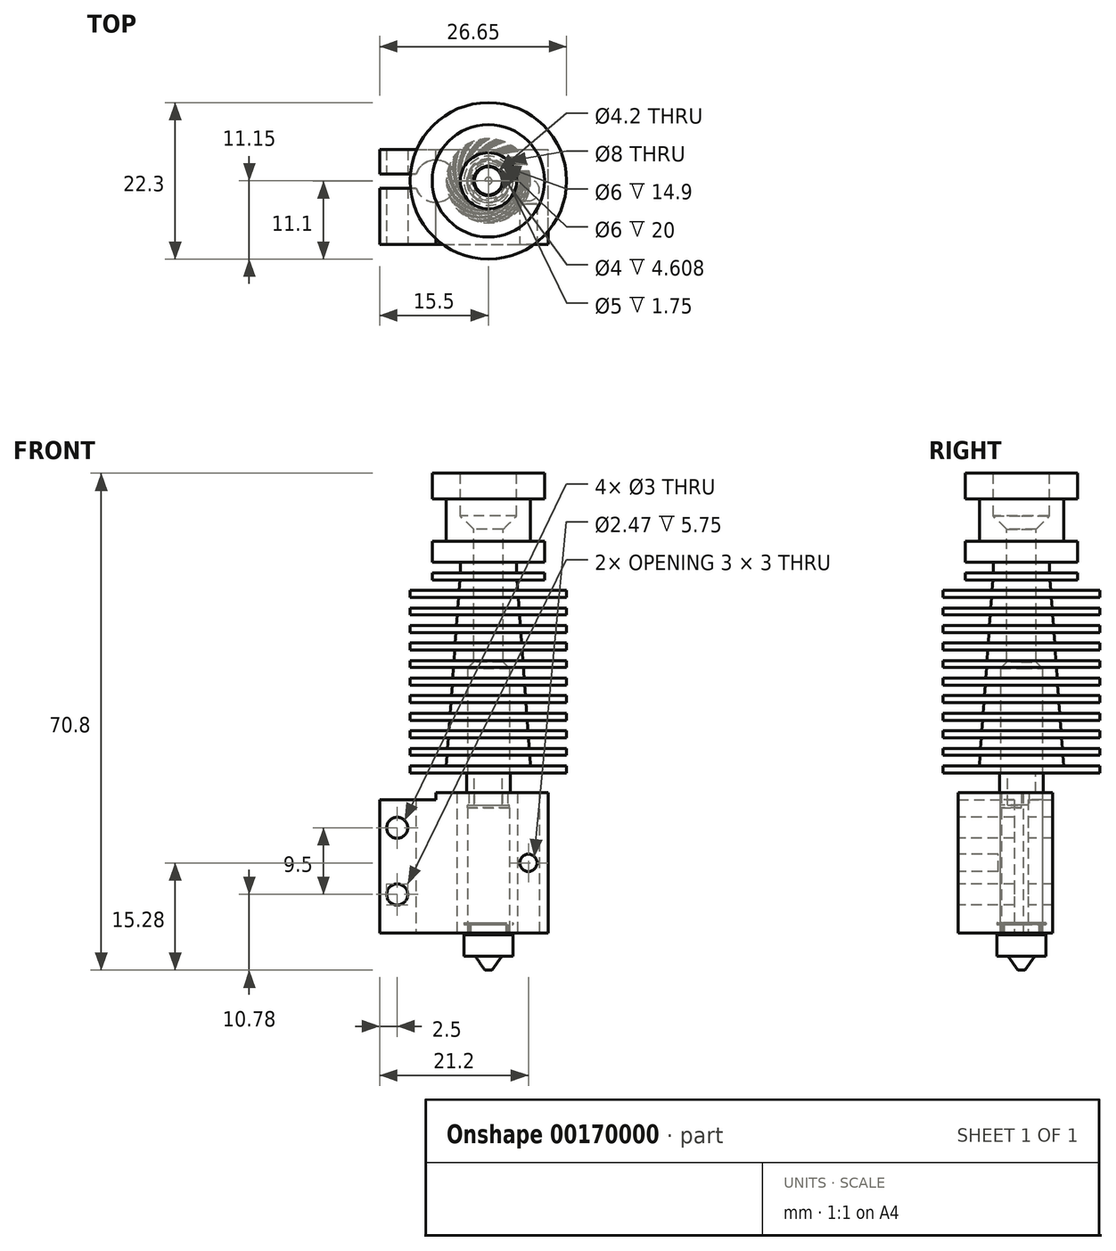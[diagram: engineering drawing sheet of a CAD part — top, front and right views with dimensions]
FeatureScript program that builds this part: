
annotation { "Feature Type Name" : "Feature", "Feature Type Description" : "" }
export const myFeature = defineFeature(function(context is Context, id is Id, definition is map)
    precondition{}
    {
        {
            var Q0;
            Q0=qCreatedBy(makeId("Top.planeOp"),FACE);
            var sketch = newSketch(context, id + "F0", { "sketchPlane" : qUnion([Q0])});
            skCircle(sketch, "E0", {"center": v(0, 0) * mm, "radius": 8 * mm});
            skSolve(sketch);
        }
        {
            var Q0;
            Q0=makeQuery(id+"F0.imprint","IMPRINT",FACE,{"disambiguationData":[TD([[makeQuery(id+"F0.imprint","IMPRINT",EDGE,{"derivedFrom":sQuery(id+"F0.wireOp",EDGE,"E0")}),1.0]])]});
            var Q1;
            Q1=sQuery(id+"F0.wireOp",EDGE,"E0");
            extrude(context, id + "F1", {"entities" : qUnion([Q0]), "surfaceEntities" : qUnion([Q1]), "oppositeDirection" : true, "depth" : 3.7 * mm});
        }
        {
            var Q0;
            Q0=makeQuery(id+"F1.opExtrude","CAP_FACE",FACE,{"disambiguationData":[OSD([sQuery(id+"F0.wireOp",EDGE,"E0")])],"isStart":false});
            var sketch = newSketch(context, id + "F2", { "sketchPlane" : qUnion([Q0])});
            skCircle(sketch, "E1", {"center": v(0, 0) * mm, "radius": 6 * mm});
            skSolve(sketch);
        }
        {
            var Q0;
            Q0=makeQuery(id+"F2.imprint","IMPRINT",FACE,{"disambiguationData":[TD([[makeQuery(id+"F2.imprint","IMPRINT",EDGE,{"derivedFrom":sQuery(id+"F2.wireOp",EDGE,"E1")}),1.0]])]});
            var Q1;
            Q1=sQuery(id+"F2.wireOp",EDGE,"E1");
            extrude(context, id + "F3", {"entities" : qUnion([Q0]), "operationType" : NewBodyOperationType.ADD, "surfaceEntities" : qUnion([Q1]), "depth" : 6 * mm});
        }
        {
            var Q0;
            Q0=makeQuery(id+"F3.opExtrude","CAP_FACE",FACE,{"disambiguationData":[OSD([sQuery(id+"F2.wireOp",EDGE,"E1")])],"isStart":false});
            var sketch = newSketch(context, id + "F4", { "sketchPlane" : qUnion([Q0])});
            skCircle(sketch, "E2", {"center": v(0, 0) * mm, "radius": 8 * mm});
            skSolve(sketch);
        }
        {
            var Q0;
            Q0=qSketchRegion(id+"F4",true);
            extrude(context, id + "F5", {"entities" : qUnion([Q0]), "operationType" : NewBodyOperationType.ADD, "depth" : 3 * mm});
        }
        {
            var Q0;
            Q0=qCreatedBy(makeId("Front.planeOp"),FACE);
            var sketch = newSketch(context, id + "F6", { "sketchPlane" : qUnion([Q0])});
            skLineSegment(sketch, "E3", {"start": v(0, 0) * mm, "end": v(0, -12.7) * mm});
            skLineSegment(sketch, "E4.bottom", {"start": v(0, -12.7) * mm, "end": v(4, -12.7) * mm});
            skLineSegment(sketch, "E4.top", {"start": v(0, -14.2) * mm, "end": v(4, -14.2) * mm});
            skLineSegment(sketch, "E4.left", {"start": v(0, -12.7) * mm, "end": v(0, -14.2) * mm});
            skLineSegment(sketch, "E4.right", {"start": v(4, -12.7) * mm, "end": v(4, -14.2) * mm});
            skLineSegment(sketch, "E5.bottom", {"start": v(0, -14.2) * mm, "end": v(8, -14.2) * mm});
            skLineSegment(sketch, "E5.top", {"start": v(0, -15.2) * mm, "end": v(8, -15.2) * mm});
            skLineSegment(sketch, "E5.left", {"start": v(0, -14.2) * mm, "end": v(0, -15.2) * mm});
            skLineSegment(sketch, "E5.right", {"start": v(8, -14.2) * mm, "end": v(8, -15.2) * mm});
            skLineSegment(sketch, "E6", {"start": v(0, -15.2) * mm, "end": v(0, -16.7) * mm});
            skLineSegment(sketch, "E7.bottom", {"start": v(0, -16.7) * mm, "end": v(11.15, -16.7) * mm});
            skLineSegment(sketch, "E7.top", {"start": v(0, -17.7) * mm, "end": v(11.15, -17.7) * mm});
            skLineSegment(sketch, "E7.left", {"start": v(0, -16.7) * mm, "end": v(0, -17.7) * mm});
            skLineSegment(sketch, "E7.right", {"start": v(11.15, -16.7) * mm, "end": v(11.15, -17.7) * mm});
            skLineSegment(sketch, "E8.1.0.0", {"start": v(0, -20.2) * mm, "end": v(11.15, -20.2) * mm});
            skLineSegment(sketch, "E8.1.0.1", {"start": v(0, -19.2) * mm, "end": v(11.15, -19.2) * mm});
            skLineSegment(sketch, "E8.1.0.2", {"start": v(0, -19.2) * mm, "end": v(0, -20.2) * mm});
            skLineSegment(sketch, "E8.1.0.3", {"start": v(11.15, -19.2) * mm, "end": v(11.15, -20.2) * mm});
            skLineSegment(sketch, "E8.2.0.0", {"start": v(0, -22.7) * mm, "end": v(11.15, -22.7) * mm});
            skLineSegment(sketch, "E8.2.0.1", {"start": v(0, -21.7) * mm, "end": v(11.15, -21.7) * mm});
            skLineSegment(sketch, "E8.2.0.2", {"start": v(0, -21.7) * mm, "end": v(0, -22.7) * mm});
            skLineSegment(sketch, "E8.2.0.3", {"start": v(11.15, -21.7) * mm, "end": v(11.15, -22.7) * mm});
            skLineSegment(sketch, "E8.3.0.0", {"start": v(0, -25.2) * mm, "end": v(11.15, -25.2) * mm});
            skLineSegment(sketch, "E8.3.0.1", {"start": v(0, -24.2) * mm, "end": v(11.15, -24.2) * mm});
            skLineSegment(sketch, "E8.3.0.2", {"start": v(0, -24.2) * mm, "end": v(0, -25.2) * mm});
            skLineSegment(sketch, "E8.3.0.3", {"start": v(11.15, -24.2) * mm, "end": v(11.15, -25.2) * mm});
            skLineSegment(sketch, "E8.4.0.0", {"start": v(0, -27.7) * mm, "end": v(11.15, -27.7) * mm});
            skLineSegment(sketch, "E8.4.0.1", {"start": v(0, -26.7) * mm, "end": v(11.15, -26.7) * mm});
            skLineSegment(sketch, "E8.4.0.2", {"start": v(0, -26.7) * mm, "end": v(0, -27.7) * mm});
            skLineSegment(sketch, "E8.4.0.3", {"start": v(11.15, -26.7) * mm, "end": v(11.15, -27.7) * mm});
            skLineSegment(sketch, "E8.5.0.0", {"start": v(0, -30.2) * mm, "end": v(11.15, -30.2) * mm});
            skLineSegment(sketch, "E8.5.0.1", {"start": v(0, -29.2) * mm, "end": v(11.15, -29.2) * mm});
            skLineSegment(sketch, "E8.5.0.2", {"start": v(0, -29.2) * mm, "end": v(0, -30.2) * mm});
            skLineSegment(sketch, "E8.5.0.3", {"start": v(11.15, -29.2) * mm, "end": v(11.15, -30.2) * mm});
            skLineSegment(sketch, "E8.6.0.0", {"start": v(0, -32.7) * mm, "end": v(11.15, -32.7) * mm});
            skLineSegment(sketch, "E8.6.0.1", {"start": v(0, -31.7) * mm, "end": v(11.15, -31.7) * mm});
            skLineSegment(sketch, "E8.6.0.2", {"start": v(0, -31.7) * mm, "end": v(0, -32.7) * mm});
            skLineSegment(sketch, "E8.6.0.3", {"start": v(11.15, -31.7) * mm, "end": v(11.15, -32.7) * mm});
            skLineSegment(sketch, "E8.7.0.0", {"start": v(0, -35.2) * mm, "end": v(11.15, -35.2) * mm});
            skLineSegment(sketch, "E8.7.0.1", {"start": v(0, -34.2) * mm, "end": v(11.15, -34.2) * mm});
            skLineSegment(sketch, "E8.7.0.2", {"start": v(0, -34.2) * mm, "end": v(0, -35.2) * mm});
            skLineSegment(sketch, "E8.7.0.3", {"start": v(11.15, -34.2) * mm, "end": v(11.15, -35.2) * mm});
            skLineSegment(sketch, "E8.8.0.0", {"start": v(0, -37.7) * mm, "end": v(11.15, -37.7) * mm});
            skLineSegment(sketch, "E8.8.0.1", {"start": v(0, -36.7) * mm, "end": v(11.15, -36.7) * mm});
            skLineSegment(sketch, "E8.8.0.2", {"start": v(0, -36.7) * mm, "end": v(0, -37.7) * mm});
            skLineSegment(sketch, "E8.8.0.3", {"start": v(11.15, -36.7) * mm, "end": v(11.15, -37.7) * mm});
            skLineSegment(sketch, "E8.9.0.0", {"start": v(0, -40.2) * mm, "end": v(11.15, -40.2) * mm});
            skLineSegment(sketch, "E8.9.0.1", {"start": v(0, -39.2) * mm, "end": v(11.15, -39.2) * mm});
            skLineSegment(sketch, "E8.9.0.2", {"start": v(0, -39.2) * mm, "end": v(0, -40.2) * mm});
            skLineSegment(sketch, "E8.9.0.3", {"start": v(11.15, -39.2) * mm, "end": v(11.15, -40.2) * mm});
            skLineSegment(sketch, "E8.10.0.0", {"start": v(0, -42.7) * mm, "end": v(11.15, -42.7) * mm});
            skLineSegment(sketch, "E8.10.0.1", {"start": v(0, -41.7) * mm, "end": v(11.15, -41.7) * mm});
            skLineSegment(sketch, "E8.10.0.2", {"start": v(0, -41.7) * mm, "end": v(0, -42.7) * mm});
            skLineSegment(sketch, "E8.10.0.3", {"start": v(11.15, -41.7) * mm, "end": v(11.15, -42.7) * mm});
            skLineSegment(sketch, "E8.direction1", {"start": v(0, -17.7) * mm, "end": v(0, -20.2) * mm, "construction": true});
            skLineSegment(sketch, "E9", {"start": v(0, -41.7) * mm, "end": v(6, -41.7) * mm});
            skLineSegment(sketch, "E10", {"start": v(4.07, -15.2) * mm, "end": v(4.18, -16.7) * mm});
            skLineSegment(sketch, "E11.trimOffspring", {"start": v(4.25, -17.7) * mm, "end": v(4.36, -19.2) * mm});
            skLineSegment(sketch, "E12.trimOffspring", {"start": v(4.44, -20.2) * mm, "end": v(4.55, -21.7) * mm});
            skLineSegment(sketch, "E13.trimOffspring", {"start": v(4.62, -22.7) * mm, "end": v(4.73, -24.2) * mm});
            skLineSegment(sketch, "E14.trimOffspring", {"start": v(4.8, -25.2) * mm, "end": v(4.9, -26.7) * mm});
            skLineSegment(sketch, "E15.trimOffspring", {"start": v(4.98, -27.7) * mm, "end": v(5.1, -29.2) * mm});
            skLineSegment(sketch, "E16.trimOffspring", {"start": v(5.16, -30.2) * mm, "end": v(5.27, -31.7) * mm});
            skLineSegment(sketch, "E17.trimOffspring", {"start": v(5.35, -32.7) * mm, "end": v(5.45, -34.2) * mm});
            skLineSegment(sketch, "E18.trimOffspring", {"start": v(5.53, -35.2) * mm, "end": v(5.64, -36.7) * mm});
            skLineSegment(sketch, "E19.trimOffspring", {"start": v(5.7, -37.7) * mm, "end": v(5.82, -39.2) * mm});
            skLineSegment(sketch, "E20.trimOffspring", {"start": v(5.9, -40.2) * mm, "end": v(6, -41.7) * mm});
            skLineSegment(sketch, "E21", {"start": v(0, -17.7) * mm, "end": v(0, -19.2) * mm});
            skLineSegment(sketch, "E22", {"start": v(0, -20.2) * mm, "end": v(0, -21.7) * mm});
            skLineSegment(sketch, "E23", {"start": v(0, -22.7) * mm, "end": v(0, -24.2) * mm});
            skLineSegment(sketch, "E24", {"start": v(0, -25.2) * mm, "end": v(0, -26.7) * mm});
            skLineSegment(sketch, "E25", {"start": v(0, -27.7) * mm, "end": v(0, -29.2) * mm});
            skLineSegment(sketch, "E26", {"start": v(0, -30.2) * mm, "end": v(0, -31.7) * mm});
            skLineSegment(sketch, "E27", {"start": v(0, -32.7) * mm, "end": v(0, -34.2) * mm});
            skLineSegment(sketch, "E28", {"start": v(0, -35.2) * mm, "end": v(0, -36.7) * mm});
            skLineSegment(sketch, "E29", {"start": v(0, -37.7) * mm, "end": v(0, -39.2) * mm});
            skLineSegment(sketch, "E30", {"start": v(0, -40.2) * mm, "end": v(0, -41.7) * mm});
            skLineSegment(sketch, "E31.right", {"start": v(3, -42.7) * mm, "end": v(3, -45.2) * mm});
            skLineSegment(sketch, "E32", {"start": v(3, -45.2) * mm, "end": v(2, -45.2) * mm});
            skLineSegment(sketch, "E33", {"start": v(2, -45.2) * mm, "end": v(2, -42.7) * mm});
            skLineSegment(sketch, "E34.bottom", {"start": v(2, -45.2) * mm, "end": v(3, -45.2) * mm});
            skLineSegment(sketch, "E34.top", {"start": v(2, -47.3) * mm, "end": v(3, -47.3) * mm});
            skLineSegment(sketch, "E34.left", {"start": v(2, -45.2) * mm, "end": v(2, -47.3) * mm});
            skLineSegment(sketch, "E34.right", {"start": v(3, -45.2) * mm, "end": v(3, -47.3) * mm});
            skLineSegment(sketch, "E35.bottom", {"start": v(3, -47.3) * mm, "end": v(3.75, -47.3) * mm});
            skLineSegment(sketch, "E35.top", {"start": v(3, -46.56) * mm, "end": v(3.75, -46.56) * mm});
            skLineSegment(sketch, "E35.left", {"start": v(3, -47.3) * mm, "end": v(3, -46.56) * mm});
            skLineSegment(sketch, "E35.right", {"start": v(3.75, -47.3) * mm, "end": v(3.75, -46.56) * mm});
            skLineSegment(sketch, "E36.bottom", {"start": v(2, -42.7) * mm, "end": v(3, -42.7) * mm});
            skLineSegment(sketch, "E36.top", {"start": v(2, -41.7) * mm, "end": v(3, -41.7) * mm});
            skLineSegment(sketch, "E36.left", {"start": v(2, -42.7) * mm, "end": v(2, -41.7) * mm});
            skLineSegment(sketch, "E36.right", {"start": v(3, -42.7) * mm, "end": v(3, -41.7) * mm});
            skSolve(sketch);
        }
        {
            var Q0;
            Q0=qSketchRegion(id+"F6",true);
            var Q1;
            {var subQ0=sQuery(id+"F6.wireOp",EDGE,"E31.right");Q1=makeQuery(id+"F6.imprint","IMPRINT",FACE,{"disambiguationData":[TD([[makeQuery(id+"F6.imprint","IMPRINT",EDGE,{"derivedFrom":subQ0}),-1.0]])]});}
            var Q2;
            Q2=makeQuery(id+"F6.imprint","IMPRINT",FACE,{"disambiguationData":[TD([[makeQuery(id+"F6.imprint","IMPRINT",EDGE,{"derivedFrom":sQuery(id+"F6.wireOp",EDGE,"E34.bottom")}),-1.0]])]});
            var Q3;
            Q3=makeQuery(id+"F6.imprint","IMPRINT",FACE,{"disambiguationData":[TD([[makeQuery(id+"F6.imprint","IMPRINT",EDGE,{"derivedFrom":sQuery(id+"F6.wireOp",EDGE,"E36.bottom")}),1.0]])]});
            var Q4;
            Q4=makeQuery(id+"F6.imprint","IMPRINT",FACE,{"disambiguationData":[TD([[makeQuery(id+"F6.imprint","IMPRINT",EDGE,{"derivedFrom":sQuery(id+"F6.wireOp",EDGE,"E31.right")}),-1.0]])]});
            var Q5;
            Q5=makeQuery(id+"F6.imprint","IMPRINT",FACE,{"disambiguationData":[TD([[makeQuery(id+"F6.imprint","IMPRINT",EDGE,{"derivedFrom":sQuery(id+"F6.wireOp",EDGE,"E34.bottom")}),-1.0]])]});
            var Q6;
            Q6=sQuery(id+"F6.wireOp",EDGE,"E3");
            revolve(context, id + "F7", {"operationType" : NewBodyOperationType.ADD, "entities" : qUnion([Q0, Q1, Q2, Q3, Q4, Q5]), "axis" : qUnion([Q6]), "revolveType" : RevolveType.FULL});
        }
        {
            var Q0;
            Q0=makeQuery(id+"F1.opExtrude","CAP_FACE",FACE,{"disambiguationData":[OSD([sQuery(id+"F0.wireOp",EDGE,"E0")])],"isStart":true});
            var sketch = newSketch(context, id + "F8", { "sketchPlane" : qUnion([Q0])});
            skCircle(sketch, "E37", {"center": v(0, 0) * mm, "radius": 2.1 * mm});
            skSolve(sketch);
        }
        {
            var Q0;
            Q0=qSketchRegion(id+"F8",true);
            extrude(context, id + "F9", {"entities" : qUnion([Q0]), "operationType" : NewBodyOperationType.REMOVE, "oppositeDirection" : true, "depth" : 42.7 * mm});
        }
        {
            var Q0;
            Q0=makeQuery(id+"F1.opExtrude","CAP_FACE",FACE,{"disambiguationData":[OSD([sQuery(id+"F0.wireOp",EDGE,"E0")])],"isStart":true});
            var sketch = newSketch(context, id + "F10", { "sketchPlane" : qUnion([Q0])});
            skCircle(sketch, "E38", {"center": v(0, 0) * mm, "radius": 4 * mm});
            skSolve(sketch);
        }
        {
            var Q0;
            Q0=qSketchRegion(id+"F10",true);
            extrude(context, id + "F11", {"entities" : qUnion([Q0]), "operationType" : NewBodyOperationType.REMOVE, "oppositeDirection" : true, "depth" : 6 * mm});
        }
        {
            var Q0;
            Q0=makeQuery(id+"F11.boolean.opBoolean","INTERSECT",EDGE,{"derivedFrom":[makeQuery(id+"F9.boolean.opBoolean","COPY",FACE,{"derivedFrom":makeQuery(id+"F9.opExtrude","SWEPT_FACE",FACE,{"disambiguationData":[OSD([sQuery(id+"F8.wireOp",EDGE,"E37")])]})}),makeQuery(id+"F11.opExtrude","CAP_FACE",FACE,{"disambiguationData":[OSD([sQuery(id+"F10.wireOp",EDGE,"E38")])],"isStart":false})]});
            chamfer(context, id + "F12", {"entities" : qUnion([Q0]), "width" : 2 * mm, "tangentPropagation" : true});
        }
        {
            var Q0;
            Q0=makeQuery(id+"F7.opRevolve","SWEPT_FACE",FACE,{"disambiguationData":[OSD([sQuery(id+"F6.wireOp",EDGE,"E8.10.0.0")])]});
            var sketch = newSketch(context, id + "F13", { "sketchPlane" : qUnion([Q0])});
            skCircle(sketch, "E39", {"center": v(0, 0) * mm, "radius": 3 * mm});
            skSolve(sketch);
        }
        {
            var Q0;
            Q0=qSketchRegion(id+"F13",true);
            extrude(context, id + "F14", {"entities" : qUnion([Q0]), "operationType" : NewBodyOperationType.REMOVE, "oppositeDirection" : true, "depth" : 14.8 * mm});
        }
        {
            var Q0;
            Q0=makeQuery(id+"F14.boolean.opBoolean","INTERSECT",EDGE,{"derivedFrom":[makeQuery(id+"F9.boolean.opBoolean","COPY",FACE,{"derivedFrom":makeQuery(id+"F9.opExtrude","SWEPT_FACE",FACE,{"disambiguationData":[OSD([sQuery(id+"F8.wireOp",EDGE,"E37")])]})}),makeQuery(id+"F14.opExtrude","CAP_FACE",FACE,{"disambiguationData":[OSD([sQuery(id+"F13.wireOp",EDGE,"E39")])],"isStart":false})]});
            chamfer(context, id + "F15", {"entities" : qUnion([Q0]), "width" : 1 * mm, "tangentPropagation" : true});
        }
        {
            var Q0;
            Q0=qCreatedBy(makeId("Front.planeOp"),FACE);
            var sketch = newSketch(context, id + "F16", { "sketchPlane" : qUnion([Q0])});
            skLineSegment(sketch, "E40.bottom", {"start": v(-7.5, -45.52) * mm, "end": v(8.5, -45.52) * mm});
            skLineSegment(sketch, "E40.top", {"start": v(-15.5, -65.52) * mm, "end": v(8.5, -65.52) * mm});
            skLineSegment(sketch, "E40.right", {"start": v(8.5, -45.52) * mm, "end": v(8.5, -65.52) * mm});
            skLineSegment(sketch, "E41", {"start": v(-15.5, -46.52) * mm, "end": v(-15.5, -65.52) * mm});
            skLineSegment(sketch, "E42", {"start": v(-7.5, -45.52) * mm, "end": v(-7.5, -46.52) * mm});
            skLineSegment(sketch, "E43", {"start": v(-15.5, -46.52) * mm, "end": v(-7.5, -46.52) * mm});
            skSolve(sketch);
        }
        {
            var Q0;
            Q0=makeQuery(id+"F16.imprint","IMPRINT",FACE,{"disambiguationData":[TD([[makeQuery(id+"F16.imprint","IMPRINT",EDGE,{"derivedFrom":sQuery(id+"F16.wireOp",EDGE,"E40.bottom")}),-1.0]])]});
            var Q1;
            Q1=makeQuery(id+"F16.imprint","IMPRINT",FACE,{"disambiguationData":[TD([[makeQuery(id+"F16.imprint","IMPRINT",EDGE,{"derivedFrom":sQuery(id+"F16.wireOp",EDGE,"hSTLO5rz-Z077-ZaO5-nEVS-phWlFBx8dYmu")}),1.0]])]});
            var Q2;
            Q2=makeQuery(id+"F16.imprint","IMPRINT",FACE,{"disambiguationData":[TD([[makeQuery(id+"F16.imprint","IMPRINT",EDGE,{"derivedFrom":sQuery(id+"F16.wireOp",EDGE,"1ucrc5hz-Jwvr-DOmE-K7qY-mdj6J8iSEPF0")}),1.0]])]});
            extrude(context, id + "F17", {"entities" : qUnion([Q0, Q1, Q2]), "depth" : 13.5 * mm, "symmetric" : true});
        }
        {
            var Q0;
            Q0=makeQuery(id+"F17.opExtrude","SWEPT_FACE",FACE,{"disambiguationData":[OSD([sQuery(id+"F16.wireOp",EDGE,"E40.top")])]});
            var sketch = newSketch(context, id + "F18", { "sketchPlane" : qUnion([Q0])});
            skCircle(sketch, "E44", {"center": v(0, -2.25) * mm, "radius": 3 * mm});
            skCircle(sketch, "E45", {"center": v(5.7, -1) * mm, "radius": 1.55 * mm});
            skArc(sketch, "E46", {"start": v(-10.33, -3.25) * mm, "mid": v(-4.5, -2.25) * mm, "end": v(-10.33, -1.25) * mm});
            skLineSegment(sketch, "E47.bottom", {"start": v(-15.5, -1.25) * mm, "end": v(-10.33, -1.25) * mm});
            skLineSegment(sketch, "E47.top", {"start": v(-15.5, -3.25) * mm, "end": v(-10.33, -3.25) * mm});
            skLineSegment(sketch, "E47.left", {"start": v(-15.5, -1.25) * mm, "end": v(-15.5, -3.25) * mm});
            skSolve(sketch);
        }
        {
            var Q0;
            Q0 = qSketchRegion(id + "F18", true);
            extrude(context, id + "F19", {"entities" : qUnion([Q0]), "operationType" : NewBodyOperationType.REMOVE, "oppositeDirection" : true, "depth" : 20 * mm});
        }
        {
            var Q0;
            Q0=makeQuery(id+"F17.opExtrude","SWEPT_BODY",BODY,{"disambiguationData":[OSD([sQuery(id+"F16.wireOp",EDGE,"E40.bottom"),sQuery(id+"F16.wireOp",EDGE,"E40.top"),sQuery(id+"F16.wireOp",EDGE,"E40.right"),sQuery(id+"F16.wireOp",EDGE,"E41"),sQuery(id+"F16.wireOp",EDGE,"E42"),sQuery(id+"F16.wireOp",EDGE,"E43")])]});
            var Q1;
            Q1=qCreatedBy(makeId("Origin.pointOp"),VERTEX);
            var Q2;
            Q2=makeQuery(id+"F19.boolean.opBoolean","COPY",EDGE,{"derivedFrom":makeQuery(id+"F19.opExtrude","CAP_EDGE",EDGE,{"disambiguationData":[OSD([sQuery(id+"F18.wireOp",EDGE,"E44")])],"isStart":true})});
            var Q3;
            Q3=qCreatedBy(makeId("Front.planeOp"),FACE);
            transform(context, id + "F20", {"entities" : qUnion([Q0]), "transformType" : TransformType.TRANSLATION_DISTANCE, "transformDirection" : qUnion([Q3]), "distance" : 2.3 * mm, "makeCopy" : false});
        }
        {
            var Q0;
            Q0=qCreatedBy(makeId("Front.planeOp"),FACE);
            var sketch = newSketch(context, id + "F21", { "sketchPlane" : qUnion([Q0])});
            skLineSegment(sketch, "E48.bottom", {"start": v(0, -65.8) * mm, "end": v(3.5, -65.8) * mm});
            skLineSegment(sketch, "E48.right", {"start": v(3.5, -65.8) * mm, "end": v(3.5, -68.8) * mm});
            skLineSegment(sketch, "E49.top", {"start": v(0, -70.8) * mm, "end": v(0.5, -70.8) * mm});
            skLineSegment(sketch, "E50", {"start": v(0.5, -70.8) * mm, "end": v(1.9, -68.8) * mm});
            skLineSegment(sketch, "E51.trimOffspring", {"start": v(1.9, -68.8) * mm, "end": v(3.5, -68.8) * mm});
            skLineSegment(sketch, "E52", {"start": v(0, -70.8) * mm, "end": v(0, -65.8) * mm});
            skLineSegment(sketch, "E53", {"start": v(0, -65.8) * mm, "end": v(2.5, -65.8) * mm});
            skLineSegment(sketch, "E54", {"start": v(2.5, -65.8) * mm, "end": v(2.5, -64.3) * mm});
            skLineSegment(sketch, "E55", {"start": v(2.5, -64.3) * mm, "end": v(2.75, -64.3) * mm});
            skLineSegment(sketch, "E56", {"start": v(2.75, -64.3) * mm, "end": v(2.75, -65.8) * mm});
            skLineSegment(sketch, "E57.bottom", {"start": v(2.5, -64.3) * mm, "end": v(3.5, -64.3) * mm});
            skLineSegment(sketch, "E57.top", {"start": v(2.5, -64.05) * mm, "end": v(3.5, -64.05) * mm});
            skLineSegment(sketch, "E57.left", {"start": v(2.5, -64.3) * mm, "end": v(2.5, -64.05) * mm});
            skLineSegment(sketch, "E57.right", {"start": v(3.5, -64.3) * mm, "end": v(3.5, -64.05) * mm});
            skSolve(sketch);
        }
        {
            var Q0;
            Q0 = qSketchRegion(id + "F21", true);
            var Q1;
            Q1=sQuery(id+"F21.wireOp",EDGE,"E52");
            revolve(context, id + "F22", {"entities" : qUnion([Q0]), "axis" : qUnion([Q1]), "revolveType" : RevolveType.FULL});
        }
        {
            var Q0;
            Q0=makeQuery(id+"F17.opExtrude","CAP_FACE",FACE,{"disambiguationData":[OSD([sQuery(id+"F16.wireOp",EDGE,"E40.bottom"),sQuery(id+"F16.wireOp",EDGE,"E40.top"),sQuery(id+"F16.wireOp",EDGE,"E40.left"),sQuery(id+"F16.wireOp",EDGE,"E40.right"),sQuery(id+"F16.wireOp",EDGE,"UV7SLQof-a04S-M22U-fSmA-h1v0EtluGPG8"),sQuery(id+"F16.wireOp",EDGE,"g7xF2yxM-ANDZ-qpWR-qvBO-6FQJMMhnbeDq.top"),sQuery(id+"F16.wireOp",EDGE,"L5R9zHDy-imt3-tSqA-0CQm-Dj3PFv1zczeX.top"),sQuery(id+"F16.wireOp",EDGE,"56c6f5e6-72b2-44f0-a3dc-ebd65ac1d403.trimOffspring")])],"isStart":false});
            var sketch = newSketch(context, id + "F23", { "sketchPlane" : qUnion([Q0])});
            skCircle(sketch, "E58", {"center": v(-13, -60.02) * mm, "radius": 1.5 * mm});
            skCircle(sketch, "E59", {"center": v(-13, -50.52) * mm, "radius": 1.5 * mm});
            skCircle(sketch, "E60", {"center": v(5.7, -55.52) * mm, "radius": 1.23 * mm});
            skSolve(sketch);
        }
        {
            var Q0;
            Q0=makeQuery(id+"F23.imprint","IMPRINT",FACE,{"disambiguationData":[TD([[makeQuery(id+"F23.imprint","IMPRINT",EDGE,{"derivedFrom":sQuery(id+"F23.wireOp",EDGE,"E60")}),1.0]])]});
            extrude(context, id + "F24", {"entities" : qUnion([Q0]), "operationType" : NewBodyOperationType.REMOVE, "oppositeDirection" : true, "depth" : 5.75 * mm});
        }
        {
            var Q0;
            Q0=makeQuery(id+"F23.imprint","IMPRINT",FACE,{"disambiguationData":[TD([[makeQuery(id+"F23.imprint","IMPRINT",EDGE,{"derivedFrom":sQuery(id+"F23.wireOp",EDGE,"E59")}),1.0]])]});
            var Q1;
            Q1=makeQuery(id+"F23.imprint","IMPRINT",FACE,{"disambiguationData":[TD([[makeQuery(id+"F23.imprint","IMPRINT",EDGE,{"derivedFrom":sQuery(id+"F23.wireOp",EDGE,"E58")}),1.0]])]});
            var Q2;
            Q2=makeQuery(id+"F17.opExtrude","CAP_FACE",FACE,{"disambiguationData":[OSD([sQuery(id+"F16.wireOp",EDGE,"E40.bottom"),sQuery(id+"F16.wireOp",EDGE,"E40.top"),sQuery(id+"F16.wireOp",EDGE,"E40.right"),sQuery(id+"F16.wireOp",EDGE,"E41"),sQuery(id+"F16.wireOp",EDGE,"E42"),sQuery(id+"F16.wireOp",EDGE,"E43")])],"isStart":true});
            extrude(context, id + "F25", {"entities" : qUnion([Q0, Q1]), "operationType" : NewBodyOperationType.REMOVE, "endBound" : BoundingType.UP_TO_SURFACE, "oppositeDirection" : true, "endBoundEntityFace" : qUnion([Q2]), "depth" : 4.5 * mm});
        }
        {
            var Q0;
            {var subQ0=sQuery(id+"F6.wireOp",EDGE,"E8.10.0.0");Q0=makeQuery(id+"F7.opRevolve","SWEPT_FACE",FACE,{"disambiguationData":[OSD([subQ0]),TDD([makeQuery(id+"F6.imprint","IMPRINT",EDGE,{"disambiguationData":[TD([[makeQuery(id+"F6.imprint","INTERSECT",VERTEX,{"derivedFrom":[subQ0,sQuery(id+"F6.wireOp",EDGE,"E8.10.0.3")]}),1.0]])],"derivedFrom":subQ0})])]});}
            var sketch = newSketch(context, id + "F26", { "sketchPlane" : qUnion([Q0])});
            skCircle(sketch, "E61", {"center": v(0, 0) * mm, "radius": 3.12 * mm});
            skSolve(sketch);
        }
        {
            var Q0;
            Q0=makeQuery(id+"F26.imprint","IMPRINT",FACE,{"disambiguationData":[TD([[makeQuery(id+"F26.imprint","IMPRINT",EDGE,{"derivedFrom":sQuery(id+"F26.wireOp",EDGE,"E61")}),1.0]])]});
            extrude(context, id + "F27", {"entities" : qUnion([Q0]), "operationType" : NewBodyOperationType.ADD, "depth" : 5 * mm});
        }
    });
